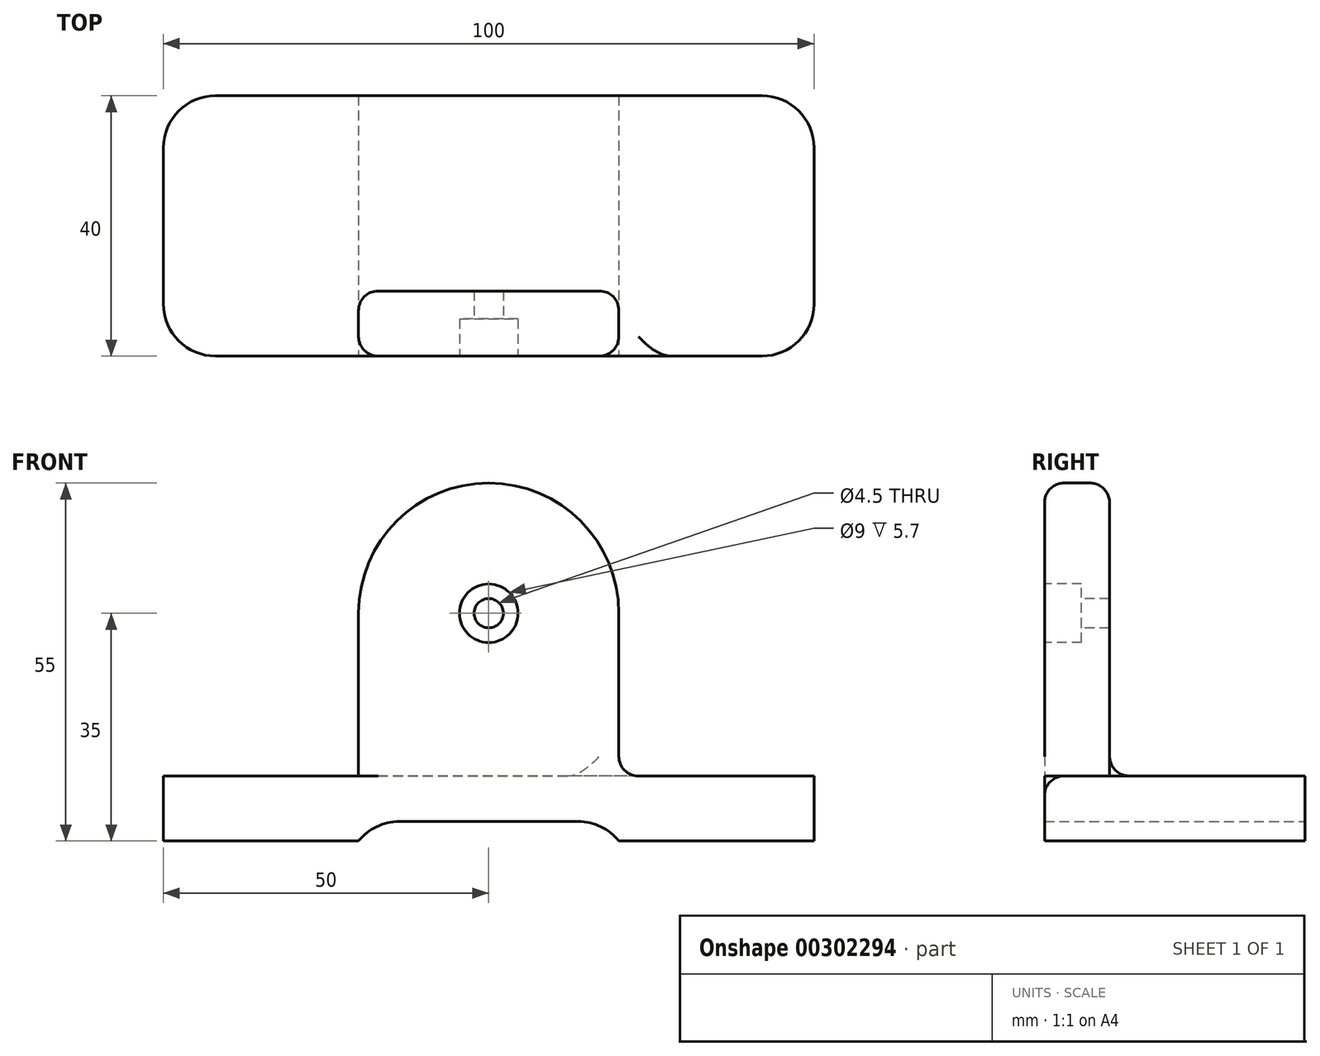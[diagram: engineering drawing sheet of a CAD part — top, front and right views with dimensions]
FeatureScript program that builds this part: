
annotation { "Feature Type Name" : "Feature", "Feature Type Description" : "" }
export const myFeature = defineFeature(function(context is Context, id is Id, definition is map)
    precondition{}
    {
        {
            var Q0;
            Q0=qCreatedBy(makeId("Top.planeOp"),FACE);
            var sketch = newSketch(context, id + "F0", { "sketchPlane" : qUnion([Q0])});
            skLineSegment(sketch, "E0.bottom", {"start": v(0, 0) * mm, "end": v(-100, 0) * mm});
            skLineSegment(sketch, "E0.top", {"start": v(0, 40) * mm, "end": v(-100, 40) * mm});
            skLineSegment(sketch, "E0.left", {"start": v(0, 0) * mm, "end": v(0, 40) * mm});
            skLineSegment(sketch, "E0.right", {"start": v(-100, 0) * mm, "end": v(-100, 40) * mm});
            skSolve(sketch);
        }
        {
            var Q0;
            Q0=makeQuery(id+"F0.imprint","IMPRINT",FACE,{"disambiguationData":[TD([[makeQuery(id+"F0.imprint","IMPRINT",EDGE,{"derivedFrom":sQuery(id+"F0.wireOp",EDGE,"E0.bottom")}),-1.0]])]});
            extrude(context, id + "F1", {"entities" : qUnion([Q0]), "depth" : 10 * mm});
        }
        {
            var Q0;
            Q0=qCreatedBy(makeId("Front.planeOp"),FACE);
            var sketch = newSketch(context, id + "F2", { "sketchPlane" : qUnion([Q0])});
            skLineSegment(sketch, "E1", {"start": v(-70, 0) * mm, "end": v(-70, 35) * mm});
            skArc(sketch, "E2", {"start": v(-70, 35) * mm, "mid": v(-50, 55) * mm, "end": v(-30, 35) * mm});
            skLineSegment(sketch, "E3", {"start": v(-30, 35) * mm, "end": v(-30, 0) * mm});
            skLineSegment(sketch, "E4", {"start": v(-30, 0) * mm, "end": v(-70, 0) * mm});
            skLineSegment(sketch, "E5", {"start": v(-70, 0) * mm, "end": v(-30, 0) * mm});
            skLineSegment(sketch, "E6", {"start": v(-50, -0.11) * mm, "end": v(-70, 0) * mm});
            skSolve(sketch);
        }
        {
            var Q0;
            Q0 = qSketchRegion(id + "F2", true);
            extrude(context, id + "F3", {"entities" : qUnion([Q0]), "operationType" : NewBodyOperationType.ADD, "oppositeDirection" : true, "depth" : 10 * mm});
        }
        {
            var Q0;
            Q0=makeQuery(id+"F3.boolean.opBoolean","MERGE",FACE,{"derivedFrom":[makeQuery(id+"F1.opExtrude","SWEPT_FACE",FACE,{"disambiguationData":[OSD([sQuery(id+"F0.wireOp",EDGE,"E0.bottom")])]}),makeQuery(id+"F3.opExtrude","CAP_FACE",FACE,{"disambiguationData":[OSD([sQuery(id+"F2.wireOp",EDGE,"E1"),sQuery(id+"F2.wireOp",EDGE,"E2"),sQuery(id+"F2.wireOp",EDGE,"E3"),sQuery(id+"F2.wireOp",EDGE,"E5")])],"isStart":true})]});
            var sketch = newSketch(context, id + "F4", { "sketchPlane" : qUnion([Q0])});
            skLineSegment(sketch, "E7.bottom", {"start": v(-70, 0) * mm, "end": v(-30, 0) * mm});
            skLineSegment(sketch, "E7.top", {"start": v(-70, 3) * mm, "end": v(-30, 3) * mm});
            skLineSegment(sketch, "E7.left", {"start": v(-70, 0) * mm, "end": v(-70, 3) * mm});
            skLineSegment(sketch, "E7.right", {"start": v(-30, 0) * mm, "end": v(-30, 3) * mm});
            skSolve(sketch);
        }
        {
            var Q0;
            Q0 = qSketchRegion(id + "F4", true);
            extrude(context, id + "F5", {"entities" : qUnion([Q0]), "operationType" : NewBodyOperationType.REMOVE, "endBound" : BoundingType.THROUGH_ALL, "oppositeDirection" : true, "depth" : 25 * mm});
        }
        {
            var Q0;
            Q0=makeQuery(id+"F3.boolean.opBoolean","MERGE",FACE,{"derivedFrom":[makeQuery(id+"F1.opExtrude","SWEPT_FACE",FACE,{"disambiguationData":[OSD([sQuery(id+"F0.wireOp",EDGE,"E0.bottom")])]}),makeQuery(id+"F3.opExtrude","CAP_FACE",FACE,{"disambiguationData":[OSD([sQuery(id+"F2.wireOp",EDGE,"E1"),sQuery(id+"F2.wireOp",EDGE,"E2"),sQuery(id+"F2.wireOp",EDGE,"E3"),sQuery(id+"F2.wireOp",EDGE,"E5")])],"isStart":true})]});
            var sketch = newSketch(context, id + "F6", { "sketchPlane" : qUnion([Q0])});
            skCircle(sketch, "E8", {"center": v(-50, 35) * mm, "radius": 2.25 * mm});
            skSolve(sketch);
        }
        {
            var Q0;
            Q0 = qSketchRegion(id + "F6", true);
            extrude(context, id + "F7", {"entities" : qUnion([Q0]), "operationType" : NewBodyOperationType.REMOVE, "depth" : 5.7 * mm});
        }
        {
            var Q0;
            Q0=makeQuery(id+"F3.boolean.opBoolean","MERGE",FACE,{"derivedFrom":[makeQuery(id+"F1.opExtrude","SWEPT_FACE",FACE,{"disambiguationData":[OSD([sQuery(id+"F0.wireOp",EDGE,"E0.bottom")])]}),makeQuery(id+"F3.opExtrude","CAP_FACE",FACE,{"disambiguationData":[OSD([sQuery(id+"F2.wireOp",EDGE,"E1"),sQuery(id+"F2.wireOp",EDGE,"E2"),sQuery(id+"F2.wireOp",EDGE,"E3"),sQuery(id+"F2.wireOp",EDGE,"E5")])],"isStart":true})]});
            var sketch = newSketch(context, id + "F8", { "sketchPlane" : qUnion([Q0])});
            skCircle(sketch, "E9", {"center": v(-50, 35) * mm, "radius": 2.25 * mm});
            skSolve(sketch);
        }
        {
            var Q0;
            Q0 = qSketchRegion(id + "F8", true);
            extrude(context, id + "F9", {"entities" : qUnion([Q0]), "operationType" : NewBodyOperationType.REMOVE, "endBound" : BoundingType.THROUGH_ALL, "oppositeDirection" : true, "depth" : 5.7 * mm});
        }
        {
            var Q0;
            Q0=makeQuery(id+"F3.boolean.opBoolean","MERGE",FACE,{"derivedFrom":[makeQuery(id+"F1.opExtrude","SWEPT_FACE",FACE,{"disambiguationData":[OSD([sQuery(id+"F0.wireOp",EDGE,"E0.bottom")])]}),makeQuery(id+"F3.opExtrude","CAP_FACE",FACE,{"disambiguationData":[OSD([sQuery(id+"F2.wireOp",EDGE,"E1"),sQuery(id+"F2.wireOp",EDGE,"E2"),sQuery(id+"F2.wireOp",EDGE,"E3"),sQuery(id+"F2.wireOp",EDGE,"E5")])],"isStart":true})]});
            var sketch = newSketch(context, id + "F10", { "sketchPlane" : qUnion([Q0])});
            skCircle(sketch, "E10", {"center": v(-50, 35) * mm, "radius": 4.5 * mm});
            skSolve(sketch);
        }
        {
            var Q0;
            Q0 = qSketchRegion(id + "F10", true);
            extrude(context, id + "F11", {"entities" : qUnion([Q0]), "operationType" : NewBodyOperationType.REMOVE, "oppositeDirection" : true, "depth" : 5.7 * mm});
        }
        {
            var Q0;
            Q0=makeQuery(id+"F5.boolean.opBoolean","COPY",EDGE,{"derivedFrom":makeQuery(id+"F5.opExtrude","SWEPT_EDGE",EDGE,{"disambiguationData":[OSD([sQuery(id+"F4.wireOp",EDGE,"E7.top"),sQuery(id+"F4.wireOp",EDGE,"E7.left")])]})});
            var Q1;
            Q1=makeQuery(id+"F5.boolean.opBoolean","COPY",EDGE,{"derivedFrom":makeQuery(id+"F5.opExtrude","SWEPT_EDGE",EDGE,{"disambiguationData":[OSD([sQuery(id+"F4.wireOp",EDGE,"E7.top"),sQuery(id+"F4.wireOp",EDGE,"E7.right")])]})});
            var Q2;
            Q2=makeQuery(id+"F1.opExtrude","SWEPT_EDGE",EDGE,{"disambiguationData":[OSD([sQuery(id+"F0.wireOp",EDGE,"E0.bottom"),sQuery(id+"F0.wireOp",EDGE,"E0.left")])]});
            var Q3;
            Q3=makeQuery(id+"F1.opExtrude","SWEPT_EDGE",EDGE,{"disambiguationData":[OSD([sQuery(id+"F0.wireOp",EDGE,"E0.top"),sQuery(id+"F0.wireOp",EDGE,"E0.left")])]});
            var Q4;
            Q4=makeQuery(id+"F1.opExtrude","SWEPT_EDGE",EDGE,{"disambiguationData":[OSD([sQuery(id+"F0.wireOp",EDGE,"E0.bottom"),sQuery(id+"F0.wireOp",EDGE,"E0.right")])]});
            var Q5;
            Q5=makeQuery(id+"F1.opExtrude","SWEPT_EDGE",EDGE,{"disambiguationData":[OSD([sQuery(id+"F0.wireOp",EDGE,"E0.top"),sQuery(id+"F0.wireOp",EDGE,"E0.right")])]});
            fillet(context, id + "F12", {"entities" : qUnion([Q0, Q1, Q2, Q3, Q4, Q5]), "radius" : 8 * mm, "tangentPropagation" : true, "allowEdgeOverflow" : false});
        }
        {
            var Q0;
            Q0=makeQuery(id+"F3.opExtrude","SWEPT_FACE",FACE,{"disambiguationData":[OSD([sQuery(id+"F2.wireOp",EDGE,"E2")])]});
            var Q1;
            Q1=makeQuery(id+"F3.boolean.opBoolean","INTERSECT",EDGE,{"derivedFrom":[makeQuery(id+"F1.opExtrude","CAP_FACE",FACE,{"disambiguationData":[OSD([sQuery(id+"F0.wireOp",EDGE,"E0.bottom"),sQuery(id+"F0.wireOp",EDGE,"E0.top"),sQuery(id+"F0.wireOp",EDGE,"E0.left"),sQuery(id+"F0.wireOp",EDGE,"E0.right")])],"isStart":false}),makeQuery(id+"F3.opExtrude","SWEPT_FACE",FACE,{"disambiguationData":[OSD([sQuery(id+"F2.wireOp",EDGE,"E3")])]})]});
            fillet(context, id + "F13", {"entities" : qUnion([Q0, Q1]), "radius" : 3 * mm, "tangentPropagation" : true, "allowEdgeOverflow" : false});
        }
        {
            var Q0;
            Q0=qCreatedBy(makeId("Front.planeOp"),FACE);
            var sketch = newSketch(context, id + "F14", { "sketchPlane" : qUnion([Q0])});
            skCircle(sketch, "E11", {"center": v(13.62, 30.42) * mm, "radius": 14.74 * mm});
            skSolve(sketch);
        }
        {
            var Q0;
            Q0=makeQuery(id+"F14.imprint","IMPRINT",FACE,{"disambiguationData":[TD([[makeQuery(id+"F14.imprint","IMPRINT",EDGE,{"derivedFrom":sQuery(id+"F14.wireOp",EDGE,"E11")}),1.0]])]});
            extrude(context, id + "F15", {"entities" : qUnion([Q0]), "depth" : 10 * mm, "offsetDistance" : 25 * mm});
        }
        {
            var Q0;
            Q0=makeQuery(id+"F15.opExtrude","CAP_EDGE",EDGE,{"disambiguationData":[OSD([sQuery(id+"F14.wireOp",EDGE,"E11")])],"isStart":true});
            fillet(context, id + "F16", {"entities" : qUnion([Q0]), "tangentPropagation" : true, "radius" : 5 * mm, "defaultsChanged" : false, "vertexSettings" : [], "allowEdgeOverflow" : false});
        }
        {
            var Q0;
            Q0=makeQuery(id+"F15.opExtrude","CAP_EDGE",EDGE,{"disambiguationData":[OSD([sQuery(id+"F14.wireOp",EDGE,"E11")])],"isStart":false});
            fillet(context, id + "F17", {"entities" : qUnion([Q0]), "tangentPropagation" : true, "radius" : 5 * mm, "defaultsChanged" : false, "vertexSettings" : [], "allowEdgeOverflow" : false});
        }
        {
            var Q0;
            Q0=makeQuery(id+"F15.opExtrude","CAP_FACE",FACE,{"disambiguationData":[OSD([sQuery(id+"F14.wireOp",EDGE,"E11")])],"isStart":true});
            var sketch = newSketch(context, id + "F18", { "sketchPlane" : qUnion([Q0])});
            skFitSpline(sketch, "E12", {"points": [v(-19.44, 32.83) * mm, v(-19.38, 34.62) * mm, v(-17.95, 35.57) * mm, v(-16.05, 35.45) * mm, v(-15.81, 32.53) * mm, v(-15.87, 32.42) * mm, v(-19.44, 32.83) * mm]});
            skFitSpline(sketch, "E13", {"points": [v(-9.92, 32.83) * mm, v(-8.02, 34.26) * mm, v(-9.69, 35.5) * mm, v(-11.53, 35.15) * mm, v(-11.95, 32.83) * mm, v(-9.92, 32.83) * mm]});
            skSolve(sketch);
        }
        {
            var Q0;
            Q0=makeQuery(id+"F18.imprint","IMPRINT",FACE,{"disambiguationData":[TD([[makeQuery(id+"F18.imprint","IMPRINT",EDGE,{"derivedFrom":sQuery(id+"F18.wireOp",EDGE,"E12")}),-1.0]])]});
            extrude(context, id + "F19", {"entities" : qUnion([Q0]), "operationType" : NewBodyOperationType.REMOVE, "oppositeDirection" : true, "depth" : 25 * mm, "offsetDistance" : 25 * mm});
        }
        {
            var Q0;
            Q0=makeQuery(id+"F15.opExtrude","CAP_FACE",FACE,{"disambiguationData":[OSD([sQuery(id+"F14.wireOp",EDGE,"E11")])],"isStart":true});
            var sketch = newSketch(context, id + "F20", { "sketchPlane" : qUnion([Q0])});
            skFitSpline(sketch, "E14", {"points": [v(-19.2, 28.83) * mm, v(-16.02, 25.75) * mm, v(-10.9, 25.3) * mm, v(-8.06, 28.86) * mm, v(-19.2, 28.83) * mm]});
            skSolve(sketch);
        }
        {
            var Q0;
            Q0=makeQuery(id+"F20.imprint","IMPRINT",FACE,{"disambiguationData":[TD([[makeQuery(id+"F20.imprint","IMPRINT",EDGE,{"derivedFrom":sQuery(id+"F20.wireOp",EDGE,"E14")}),1.0]])]});
            extrude(context, id + "F21", {"entities" : qUnion([Q0]), "operationType" : NewBodyOperationType.REMOVE, "oppositeDirection" : true, "depth" : 25 * mm, "offsetDistance" : 25 * mm});
        }
        {
            var Q0;
            Q0=makeQuery(id+"F15.opExtrude","CAP_FACE",FACE,{"disambiguationData":[OSD([sQuery(id+"F14.wireOp",EDGE,"E11")])],"isStart":true});
            var sketch = newSketch(context, id + "F22", { "sketchPlane" : qUnion([Q0])});
            skFitSpline(sketch, "E15", {"points": [v(-11.57, 32.49) * mm, v(-8.25, 32.49) * mm, v(-8.25, 34.63) * mm, v(-11.62, 35.6) * mm, v(-12.67, 32.49) * mm, v(-11.57, 32.49) * mm]});
            skSolve(sketch);
        }
        {
            var Q0;
            Q0=makeQuery(id+"F22.imprint","IMPRINT",FACE,{"disambiguationData":[TD([[makeQuery(id+"F22.imprint","IMPRINT",EDGE,{"derivedFrom":sQuery(id+"F22.wireOp",EDGE,"E15")}),1.0]])]});
            extrude(context, id + "F23", {"entities" : qUnion([Q0]), "operationType" : NewBodyOperationType.REMOVE, "oppositeDirection" : true, "depth" : 25 * mm, "offsetDistance" : 25 * mm});
        }
        {
            var Q0;
            Q0=makeQuery(id+"F15.opExtrude","SWEPT_BODY",BODY,{"disambiguationData":[OSD([sQuery(id+"F14.wireOp",EDGE,"E11")])]});
            deleteBodies(context, id + "F24", {"entities" : qUnion([Q0])});
        }
    });
